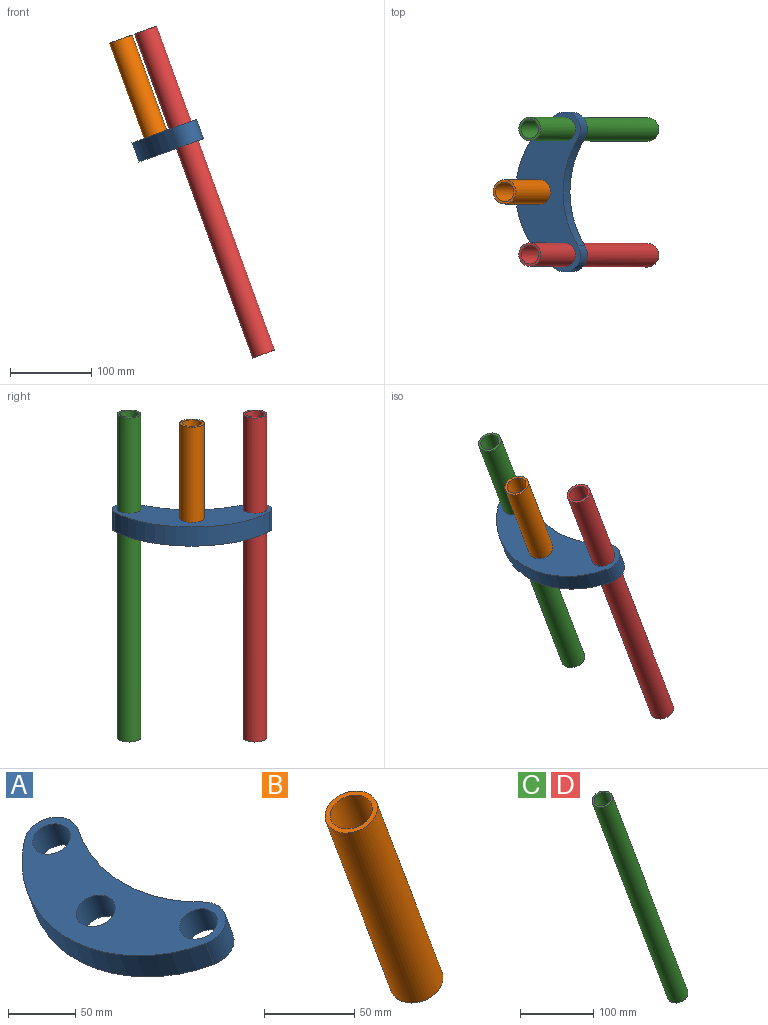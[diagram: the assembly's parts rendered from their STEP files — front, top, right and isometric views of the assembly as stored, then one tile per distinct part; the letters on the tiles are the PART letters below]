
ASSEMBLY  parts=4 mates=1
PART A: 9 faces, bbox 88.4x197x52.6 mm
  f0: cylinder r=21mm len=38.73mm, axis (-0.34,0,0.94), area 1420.4mm2, adj f1,f4,f7,f8
  f1: cylinder r=121.11mm len=132.09mm, axis (-0.34,0,0.94), area 3492.9mm2, adj f0,f2,f7,f8
  f2: cylinder r=21mm len=38.73mm, axis (-0.34,0,0.94), area 1420.4mm2, adj f1,f4,f7,f8
  f3: cylinder r=15mm len=36.74mm, axis (-0.34,0,0.94), area 2356.2mm2, adj f7,f8
  f4: cylinder r=112.35mm len=190.63mm, axis (-0.34,0,0.94), area 5690.2mm2, adj f0,f2,f7,f8
  f5: cylinder r=14.5mm len=35.8mm, axis (-0.34,0,0.94), area 2277.7mm2, adj f7,f8
  f6: cylinder r=14.5mm len=35.8mm, axis (-0.34,0,0.94), area 2277.7mm2, adj f7,f8
  f7: plane 197x79.87mm, normal (0.34,0,-0.94), area 8974.5mm2, adj f0,f1,f2,f3,f4,f5,f6
  f8: plane 197x79.87mm, normal (-0.34,0,0.94), area 8974.5mm2, adj f0,f1,f2,f3,f4,f5,f6
PART B: 4 faces, bbox 79.5x30x151.2 mm
  f0: cylinder r=12mm len=149.16mm, axis (0.34,0,-0.94), area 11309.7mm2, adj f2,f3
  f1: cylinder r=15mm len=151.21mm, axis (0.34,0,-0.94), area 14137.2mm2, adj f2,f3
  f2: plane 30x28.19mm, normal (-0.34,0,0.94), area 254.5mm2, adj f0,f1
  f3: plane 30x28.19mm, normal (0.34,0,-0.94), area 254.5mm2, adj f0,f1
PART C: 4 faces, bbox 172.6x29x409.3 mm
  f0: cylinder r=11.5mm len=407.24mm, axis (0.34,0,-0.94), area 30709.1mm2, adj f2,f3
  f1: cylinder r=14.5mm len=409.29mm, axis (0.34,0,-0.94), area 38720.1mm2, adj f2,f3
  f2: plane 29x27.25mm, normal (0.34,0,-0.94), area 245mm2, adj f0,f1
  f3: plane 29x27.25mm, normal (-0.34,0,0.94), area 245mm2, adj f0,f1
PART D: same geometry as C
PLACE A at identity
PLACE B at identity fixed
PLACE C t=(0,155,0)mm
PLACE D at identity
MATE fastened C.f0 <-> A.f2  axis (-0.34,0,0.94) through (-115.59,77.5,415.53)mm
